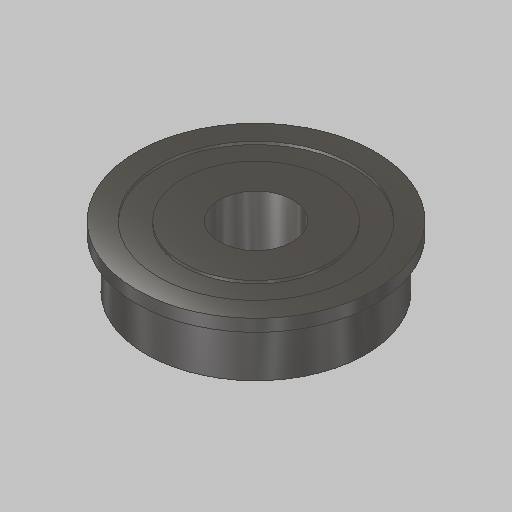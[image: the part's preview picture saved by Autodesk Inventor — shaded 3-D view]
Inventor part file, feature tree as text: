
AUTODESK INVENTOR PART (.ipt)
format: ipt  version: 2023.5 (Build 275446000, 446)  size: 134,656 bytes
history: native  units: in
note: dims shown in document units (in); Inventor stores cm internally (conversion verified against a paired STEP export)
features: revolve x1
ambient origin geometry x8: Origin, YZ Plane, XZ Plane, XY Plane, X Axis, Y Axis, Z Axis, Center Point
bodies: Solid1 (feature_tree)
feature tree (1):
  revolve  "Revolve1"  [1 undecoded]
note: 1 required parameter value undecoded (feature->parameter linkage not recoverable at this tier; creation-order binding heuristic only, values carry confidence <= 0.55)
